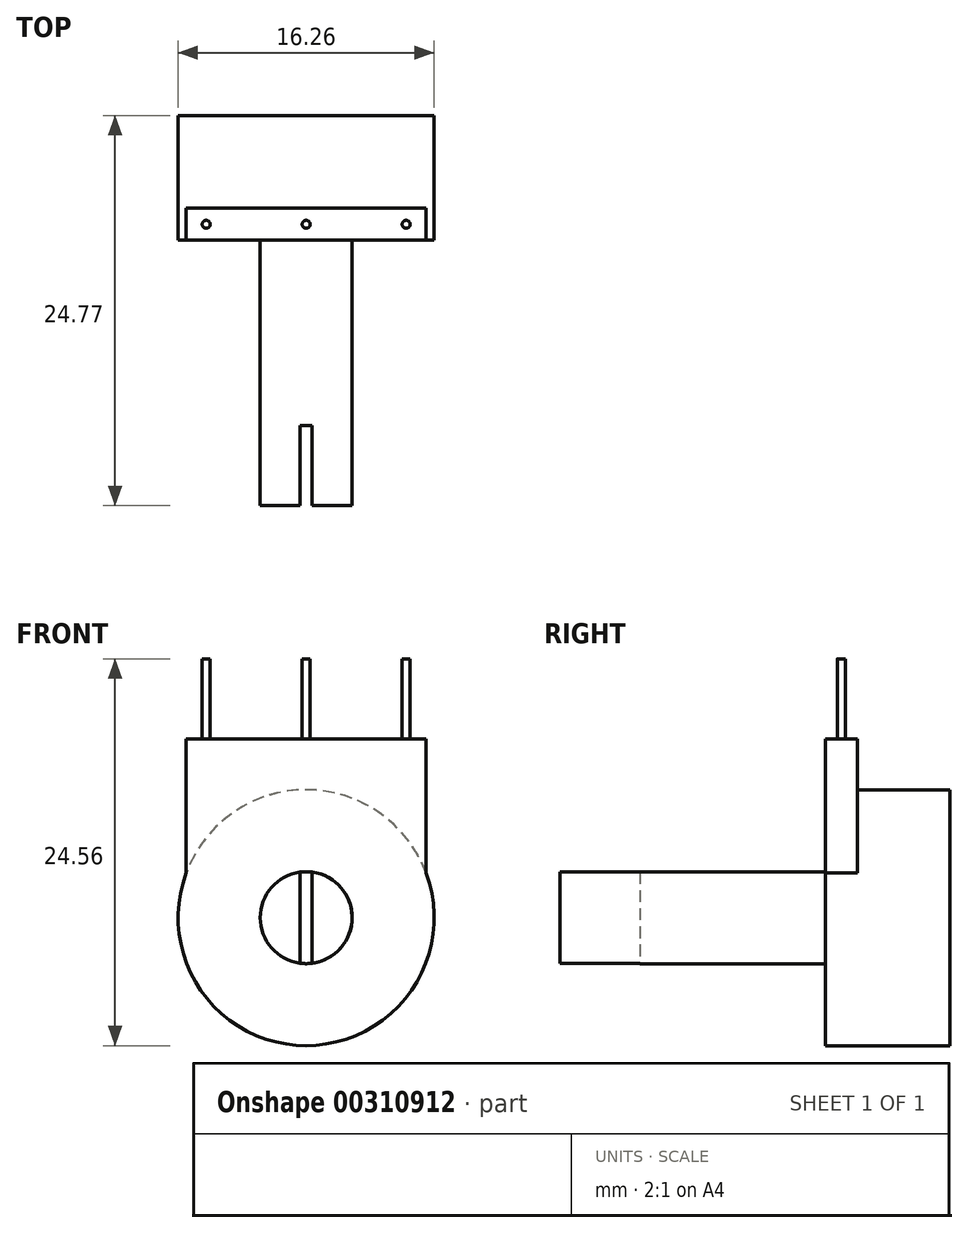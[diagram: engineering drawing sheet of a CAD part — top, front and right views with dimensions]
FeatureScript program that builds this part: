
annotation { "Feature Type Name" : "Feature", "Feature Type Description" : "" }
export const myFeature = defineFeature(function(context is Context, id is Id, definition is map)
    precondition{}
    {
        {
            var Q0;
            Q0=qCreatedBy(makeId("Front.planeOp"),FACE);
            var sketch = newSketch(context, id + "F0", { "sketchPlane" : qUnion([Q0])});
            skCircle(sketch, "E0", {"center": v(0, 0) * mm, "radius": 8.13 * mm});
            skSolve(sketch);
        }
        {
            var Q0;
            Q0 = qSketchRegion(id + "F0", true);
            extrude(context, id + "F1", {"entities" : qUnion([Q0]), "depth" : 7.92 * mm});
        }
        {
            var Q0;
            Q0=makeQuery(id+"F1.opExtrude","CAP_FACE",FACE,{"disambiguationData":[OSD([sQuery(id+"F0.wireOp",EDGE,"E0")])],"isStart":false});
            var sketch = newSketch(context, id + "F2", { "sketchPlane" : qUnion([Q0])});
            skCircle(sketch, "E1", {"center": v(0, 0) * mm, "radius": 2.92 * mm});
            skSolve(sketch);
        }
        {
            var Q0;
            Q0 = qSketchRegion(id + "F2", true);
            extrude(context, id + "F3", {"entities" : qUnion([Q0]), "operationType" : NewBodyOperationType.ADD, "depth" : 16.84 * mm});
        }
        {
            var Q0;
            Q0=makeQuery(id+"F1.opExtrude","CAP_FACE",FACE,{"disambiguationData":[OSD([sQuery(id+"F0.wireOp",EDGE,"E0")])],"isStart":false});
            var sketch = newSketch(context, id + "F4", { "sketchPlane" : qUnion([Q0])});
            skLineSegment(sketch, "E2.bottom", {"start": v(7.62, 11.35) * mm, "end": v(-7.62, 11.35) * mm});
            skLineSegment(sketch, "E2.top", {"start": v(7.62, 0.5) * mm, "end": v(-7.62, 0.5) * mm});
            skLineSegment(sketch, "E2.left", {"start": v(7.62, 11.35) * mm, "end": v(7.62, 0.5) * mm});
            skLineSegment(sketch, "E2.right", {"start": v(-7.62, 11.35) * mm, "end": v(-7.62, 0.5) * mm});
            skPoint(sketch, "E2.middle", {"position": v(0, 5.93) * mm});
            skSolve(sketch);
        }
        {
            var Q0;
            Q0 = qSketchRegion(id + "F4", true);
            extrude(context, id + "F5", {"entities" : qUnion([Q0]), "operationType" : NewBodyOperationType.ADD, "oppositeDirection" : true, "depth" : 2.03 * mm});
        }
        {
            var Q0;
            Q0=makeQuery(id+"F5.opExtrude","SWEPT_FACE",FACE,{"disambiguationData":[OSD([sQuery(id+"F4.wireOp",EDGE,"E2.bottom")])]});
            var sketch = newSketch(context, id + "F6", { "sketchPlane" : qUnion([Q0])});
            skCircle(sketch, "E3", {"center": v(0, -6.9) * mm, "radius": 0.25 * mm});
            skCircle(sketch, "E4", {"center": v(6.35, -6.9) * mm, "radius": 0.25 * mm});
            skCircle(sketch, "E5", {"center": v(-6.35, -6.9) * mm, "radius": 0.25 * mm});
            skLineSegment(sketch, "E6", {"start": v(-7.62, -6.9) * mm, "end": v(7.62, -6.9) * mm, "construction": true});
            skSolve(sketch);
        }
        {
            var Q0;
            Q0 = qSketchRegion(id + "F6", true);
            extrude(context, id + "F7", {"entities" : qUnion([Q0]), "operationType" : NewBodyOperationType.ADD, "depth" : 5.08 * mm});
        }
        {
            var Q0;
            Q0=makeQuery(id+"F3.opExtrude","CAP_FACE",FACE,{"disambiguationData":[OSD([sQuery(id+"F2.wireOp",EDGE,"E1")])],"isStart":false});
            var sketch = newSketch(context, id + "F8", { "sketchPlane" : qUnion([Q0])});
            skLineSegment(sketch, "E7.bottom", {"start": v(0.38, 3.18) * mm, "end": v(-0.38, 3.18) * mm});
            skLineSegment(sketch, "E7.top", {"start": v(0.38, -3.18) * mm, "end": v(-0.38, -3.18) * mm});
            skLineSegment(sketch, "E7.left", {"start": v(0.38, 3.18) * mm, "end": v(0.38, -3.18) * mm});
            skLineSegment(sketch, "E7.right", {"start": v(-0.38, 3.18) * mm, "end": v(-0.38, -3.17) * mm});
            skPoint(sketch, "E7.middle", {"position": v(0, 0) * mm});
            skSolve(sketch);
        }
        {
            var Q0;
            Q0 = qSketchRegion(id + "F8", true);
            extrude(context, id + "F9", {"entities" : qUnion([Q0]), "operationType" : NewBodyOperationType.REMOVE, "oppositeDirection" : true, "depth" : 5.08 * mm});
        }
    });
